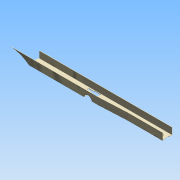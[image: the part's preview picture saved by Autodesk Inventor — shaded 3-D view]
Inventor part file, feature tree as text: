
AUTODESK INVENTOR PART (.ipt)
format: ipt  version: 2015 (Build 190159000, 159)  size: 184,320 bytes
history: native  units: mm
features: extrude x6, sketch x6, shell x1, pattern_linear x1, fillet x1
ambient origin geometry x8: Origin, YZ Plane, XZ Plane, XY Plane, X Axis, Y Axis, Z Axis, Center Point
bodies: 实体1 (feature_tree)
feature tree (15):
  extrude  "拉伸1"  Depth=80.0mm
  extrude  "拉伸2"  Depth=10.0mm
  shell  "抽壳1"  Thickness=10.0mm
  extrude  "拉伸3"  Depth=50.0mm
  pattern_linear  "矩形阵列1"  Count1=2  [1 undecoded]
  extrude  "拉伸4"  Depth=5.0mm
  extrude  "拉伸5"  Depth=3.0mm
  fillet  "圆角1"  Radius=5.0mm
  extrude  "拉伸6"  Depth=10.0mm
  sketch  "草图1"  dims[d0=950.0mm d1=80.0mm]
  sketch  "草图2"  dims[d2=250.0mm d3=200.0mm d4=10.0mm]
  sketch  "草图3"  dims[d5=50.0mm d6=0.0mm d7=40.0mm d8=20.0mm]
  sketch  "草图4"  dims[d9=135.0deg d10=5.0mm]
  sketch  "草图5"  dims[d11=950.0mm d12=0.0mm d13=3.0mm d14=5.0mm]
  sketch  "草图6"  dims[d15=25.0mm d16=40.0mm d17=25.0mm d18=0.0mm d19=100.0mm d21=100.0mm d22=525.0mm d23=25.0mm d25=120.0deg d26=73.0mm d27=0.0mm d28=150.0mm d29=3.0mm d30=0.0mm d31=3.0mm d32=17.0mm d33=32.0mm d34=11.0mm d35=10.0mm d36=0.0mm]
note: 1 required parameter value undecoded (feature->parameter linkage not recoverable at this tier; creation-order binding heuristic only, values carry confidence <= 0.55)
